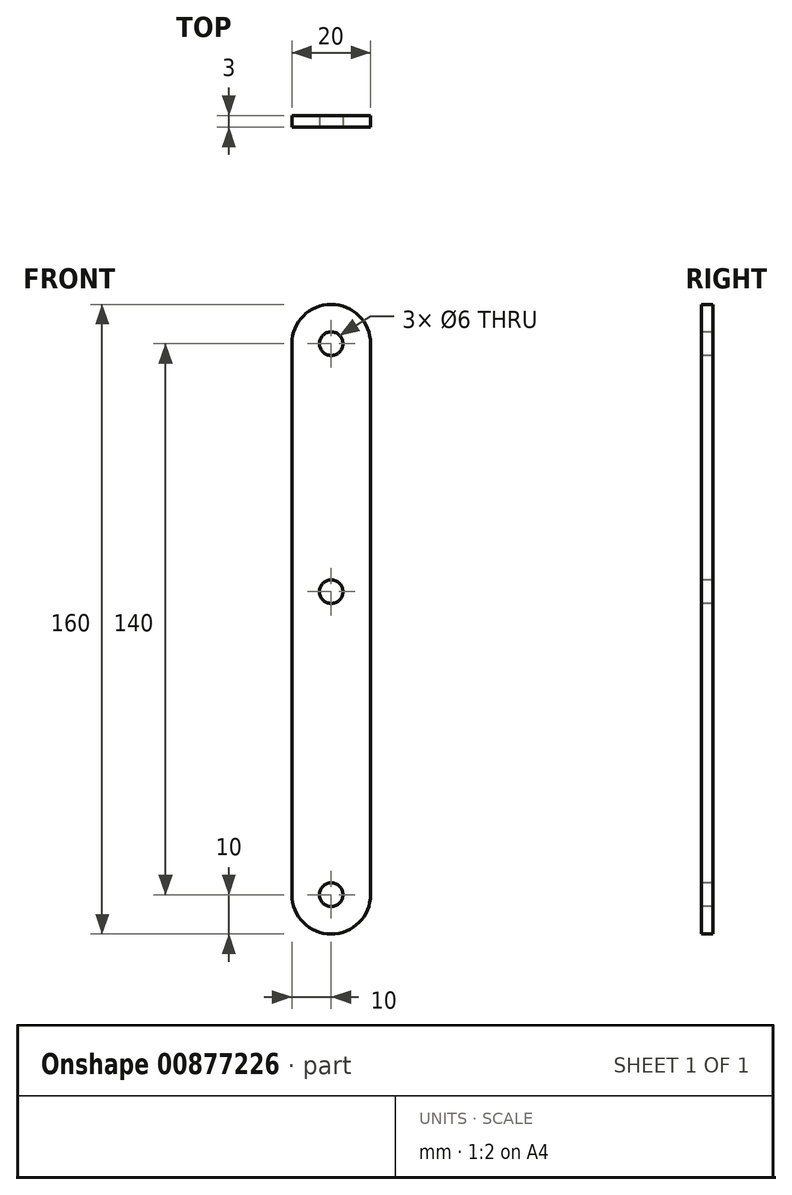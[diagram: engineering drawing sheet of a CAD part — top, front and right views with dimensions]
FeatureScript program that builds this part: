
annotation { "Feature Type Name" : "Feature", "Feature Type Description" : "" }
export const myFeature = defineFeature(function(context is Context, id is Id, definition is map)
    precondition{}
    {
        {
            var Q0;
            Q0=qCreatedBy(makeId("Front.planeOp"),FACE);
            var sketch = newSketch(context, id + "F0", { "sketchPlane" : qUnion([Q0])});
            skCircle(sketch, "E0", {"center": v(0, 80) * mm, "radius": 10 * mm});
            skCircle(sketch, "E1", {"center": v(0, -60) * mm, "radius": 10 * mm});
            skLineSegment(sketch, "E2", {"start": v(10, 80) * mm, "end": v(10, -60) * mm});
            skLineSegment(sketch, "E3", {"start": v(-10, 80) * mm, "end": v(-10, -60) * mm});
            skSolve(sketch);
        }
        {
            var Q0;
            Q0 = qSketchRegion(id + "F0", true);
            extrude(context, id + "F1", {"entities" : qUnion([Q0]), "depth" : 3 * mm, "offsetDistance" : 25.4 * mm});
        }
        {
            var Q0;
            Q0=makeQuery(id+"F1.opExtrude","CAP_FACE",FACE,{"disambiguationData":[OSD([sQuery(id+"F0.wireOp",EDGE,"E0"),sQuery(id+"F0.wireOp",EDGE,"E1"),sQuery(id+"F0.wireOp",EDGE,"E2"),sQuery(id+"F0.wireOp",EDGE,"E3")])],"isStart":false});
            var sketch = newSketch(context, id + "F2", { "sketchPlane" : qUnion([Q0])});
            skCircle(sketch, "E4", {"center": v(0, 80) * mm, "radius": 3 * mm});
            skCircle(sketch, "E5", {"center": v(0, -60) * mm, "radius": 3 * mm});
            skSolve(sketch);
        }
        {
            var Q0;
            Q0 = qSketchRegion(id + "F2", true);
            extrude(context, id + "F3", {"entities" : qUnion([Q0]), "operationType" : NewBodyOperationType.REMOVE, "oppositeDirection" : true, "depth" : 25.4 * mm, "offsetDistance" : 25.4 * mm});
        }
        {
            var Q0;
            Q0=makeQuery(id+"F1.opExtrude","CAP_FACE",FACE,{"disambiguationData":[OSD([sQuery(id+"F0.wireOp",EDGE,"E0"),sQuery(id+"F0.wireOp",EDGE,"E1"),sQuery(id+"F0.wireOp",EDGE,"E2"),sQuery(id+"F0.wireOp",EDGE,"E3")])],"isStart":false});
            var sketch = newSketch(context, id + "F4", { "sketchPlane" : qUnion([Q0])});
            skCircle(sketch, "E6", {"center": v(0, 17) * mm, "radius": 3 * mm});
            skSolve(sketch);
        }
        {
            var Q0;
            Q0=makeQuery(id+"F4.imprint","IMPRINT",FACE,{"disambiguationData":[TD([[makeQuery(id+"F4.imprint","IMPRINT",EDGE,{"derivedFrom":sQuery(id+"F4.wireOp",EDGE,"E6")}),1.0]])]});
            extrude(context, id + "F5", {"entities" : qUnion([Q0]), "operationType" : NewBodyOperationType.REMOVE, "oppositeDirection" : true, "depth" : 25 * mm, "offsetDistance" : 25 * mm});
        }
    });
